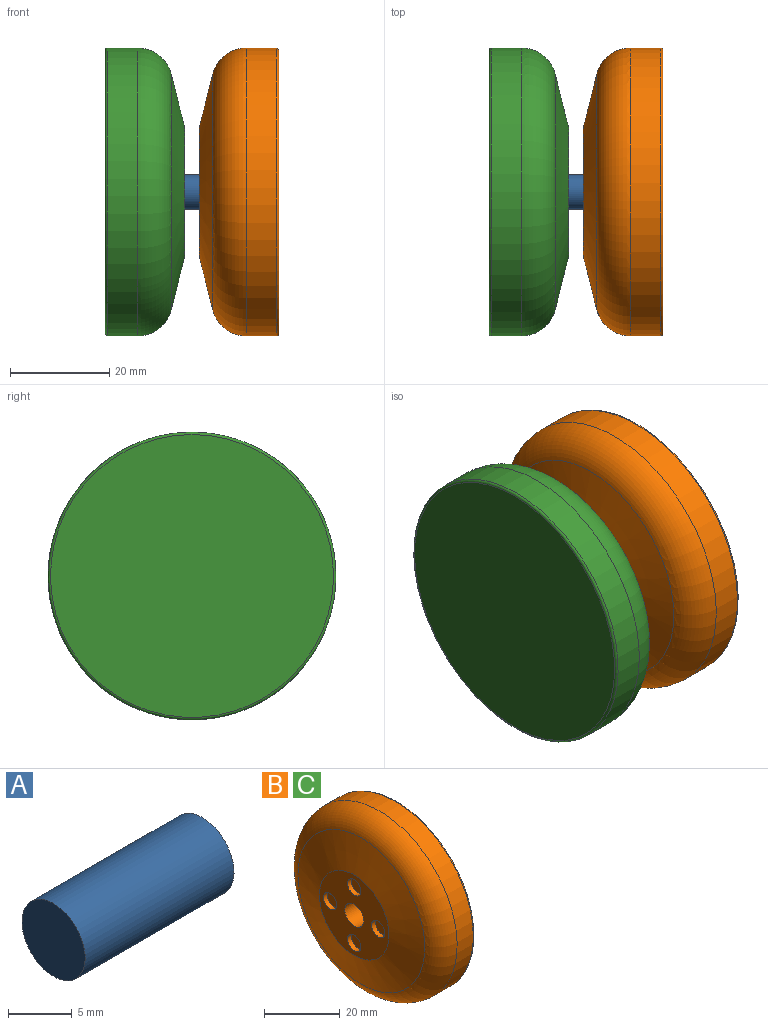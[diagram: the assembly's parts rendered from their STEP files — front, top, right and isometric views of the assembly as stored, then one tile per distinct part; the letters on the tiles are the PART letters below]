
ASSEMBLY  parts=3 mates=1
PART A: 3 faces, bbox 16.5x7x7 mm
  f0: plane 7x7mm, normal (1,0,0), area 38.5mm2, adj f1
  f1: cylinder r=3.5mm len=16.5mm, axis (-1,0,0), area 362.9mm2, adj f0,f2
  f2: plane 7x7mm, normal (-1,0,0), area 38.5mm2, adj f1
PART B: 16 faces, bbox 16x62.8x62.8 mm
  f0: plane 26x26mm, normal (-1,0,0), area 413.9mm2, adj f1,f5,f8,f10,f12,f14
  f1: cylinder r=3.5mm len=7mm, axis (-1,0,0), area 148.4mm2, adj f0,f2
  f2: plane 7x7mm, normal (-1,0,0), area 38.5mm2, adj f1
  f3: plane 57x57mm, normal (1,0,0), area 2551.8mm2, adj f7
  f4: cylinder r=29mm len=58mm, axis (-1,0,0), area 1099.6mm2, adj f6,f7
  f5: cone r=29mm half-angle=76deg, axis (1,0,0), area 1271.3mm2, adj f0,f6
  f6: torus R=22mm, axis (1,0,0), area 1581.6mm2, adj f4,f5
  f7: torus R=28.5mm, axis (1,0,0), area 142.2mm2, adj f3,f4
  f8: cylinder r=2.5mm len=5mm, axis (-1,0,0), area 23.6mm2, adj f0,f9
  f9: plane 5x5mm, normal (-1,0,0), area 19.6mm2, adj f8
  f10: cylinder r=2.5mm len=5mm, axis (-1,0,0), area 23.6mm2, adj f0,f11
  f11: plane 5x5mm, normal (-1,0,0), area 19.6mm2, adj f10
  f12: cylinder r=2.5mm len=5mm, axis (-1,0,0), area 23.6mm2, adj f0,f13
  f13: plane 5x5mm, normal (-1,0,0), area 19.6mm2, adj f12
  f14: cylinder r=2.5mm len=5mm, axis (-1,0,0), area 23.6mm2, adj f0,f15
  f15: plane 5x5mm, normal (-1,0,0), area 19.6mm2, adj f14
PART C: same geometry as B
PLACE A at identity
PLACE B at identity
PLACE C rot(axis=(0,1,0),180deg) t=(0,0,0)mm
MATE slider C.f1 <-> A.f1  axis (1,0,0) through (-8.25,0,0)mm
